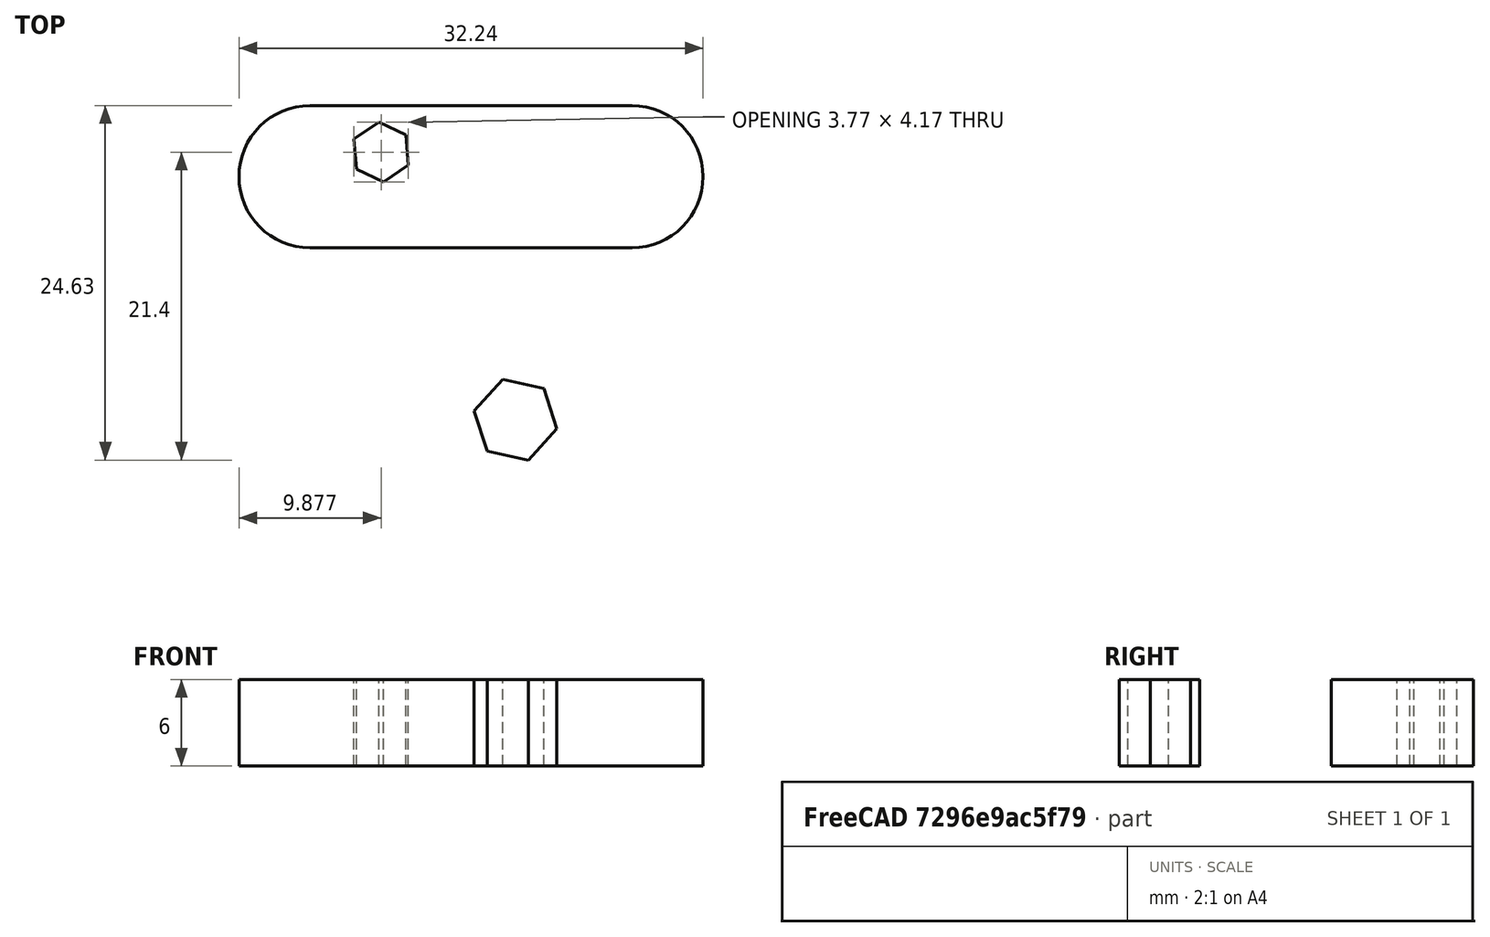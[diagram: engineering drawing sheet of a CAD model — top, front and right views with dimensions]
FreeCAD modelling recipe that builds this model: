
FCSTD DOCUMENT  (FreeCAD 0.18R16131 (Git))
Label: someModel_2
License: All rights reserved
LicenseURL: http://en.wikipedia.org/wiki/All_rights_reserved
objects: Sketcher::SketchObject×1, PartDesign::Body×1, Part::Extrusion×1
note: 3 computed .brp shape members not serialized (recipe doc carries the construction recipe); baked Part::Feature solids carry a one-line shape summary decoded from their .brp

FEATURE [Sketcher::SketchObject] Sketch
  MapMode = 5
  Support = -> [XY_Plane]
  sketch-geometry (18):
    g0: ArcOfCircle CenterX=7.49734 CenterY=-6.42657 CenterZ=0 NormalX=0 NormalY=0 NormalZ=1 AngleXU=0 Radius=4.93987 StartAngle=1.5708 EndAngle=4.71239
    g1: ArcOfCircle CenterX=29.8615 CenterY=-6.42657 CenterZ=0 NormalX=0 NormalY=0 NormalZ=1 AngleXU=0 Radius=4.93987 StartAngle=4.71239 EndAngle=7.85398
    g2: LineSegment StartX=7.49734 StartY=-11.3664 StartZ=0 EndX=29.8615 EndY=-11.3664 EndZ=0
    g3: LineSegment StartX=7.49734 StartY=-1.4867 StartZ=0 EndX=29.8615 EndY=-1.4867 EndZ=0
    g4: LineSegment StartX=14.3233 StartY=-5.61823 StartZ=0 EndX=14.1581 EndY=-3.53571 EndZ=0
    g5: LineSegment StartX=14.1581 StartY=-3.53571 StartZ=0 EndX=12.272 EndY=-2.63755 EndZ=0
    g6: LineSegment StartX=12.272 StartY=-2.63755 StartZ=0 EndX=10.5511 EndY=-3.82191 EndZ=0
    g7: LineSegment StartX=10.5511 StartY=-3.82191 StartZ=0 EndX=10.7163 EndY=-5.90443 EndZ=0
    g8: LineSegment StartX=10.7163 StartY=-5.90443 StartZ=0 EndX=12.6024 EndY=-6.80259 EndZ=0
    g9: LineSegment StartX=12.6024 StartY=-6.80259 StartZ=0 EndX=14.3233 EndY=-5.61823 EndZ=0
    g10: Circle [constr] CenterX=12.4372 CenterY=-4.72007 CenterZ=0 NormalX=0 NormalY=0 NormalZ=1 AngleXU=0 Radius=2.08906
    g11: LineSegment StartX=24.6522 StartY=-23.9407 StartZ=0 EndX=23.7596 EndY=-21.1373 EndZ=0
    g12: LineSegment StartX=23.7596 StartY=-21.1373 StartZ=0 EndX=20.8855 EndY=-20.5085 EndZ=0
    g13: LineSegment StartX=20.8855 StartY=-20.5085 StartZ=0 EndX=18.9039 EndY=-22.6832 EndZ=0
    g14: LineSegment StartX=18.9039 StartY=-22.6832 StartZ=0 EndX=19.7965 EndY=-25.4866 EndZ=0
    g15: LineSegment StartX=19.7965 StartY=-25.4866 StartZ=0 EndX=22.6706 EndY=-26.1154 EndZ=0
    g16: LineSegment StartX=22.6706 StartY=-26.1154 StartZ=0 EndX=24.6522 EndY=-23.9407 EndZ=0
    g17: Circle [constr] CenterX=21.7781 CenterY=-23.312 CenterZ=0 NormalX=0 NormalY=0 NormalZ=1 AngleXU=0 Radius=2.94207
  constraints (32):
    c: Tangent(g0,g3) = 1.5708
    c: Tangent(g0,g2) = -1.5708
    c: Tangent(g2,g1) = -1.5708
    c: Tangent(g3,g1) = 1.5708
    c: Horizontal(g2)
    c: Equal(g0,g1)
    c: Coincident(g4,g5)
    c: Coincident(g5,g6)
    c: Coincident(g6,g7)
    c: Coincident(g7,g8)
    c: Coincident(g8,g9)
    c: Coincident(g9,g4)
    c: Equal(g4, g5-g9) x5
    c: PointOnObject(g4,g10)
    c: PointOnObject(g5,g10)
    c: PointOnObject(g6,g10)
    c: PointOnObject(g7,g10)
    c: PointOnObject(g8,g10)
    c: PointOnObject(g9,g10)
    c: Coincident(g11,g12)
    c: Coincident(g12,g13)
    c: Coincident(g13,g14)
    c: Coincident(g14,g15)
    c: Coincident(g15,g16)
    c: Coincident(g16,g11)
    c: Equal(g11, g12-g16) x5
    c: PointOnObject(g11,g17)
    c: PointOnObject(g12,g17)
    c: PointOnObject(g13,g17)
    c: PointOnObject(g14,g17)
    c: PointOnObject(g15,g17)
    c: PointOnObject(g16,g17)
FEATURE [PartDesign::Body] Body
  Group = -> [Sketch]
  Origin = -> Origin
FEATURE [Part::Extrusion] Extrude
  Base = -> Sketch
  Dir = (0,0,1)
  DirMode = 2
  FaceMakerClass = Part::FaceMakerBullseye
  LengthFwd = 6
  LengthRev = 0
  Solid = true
  Symmetric = false
